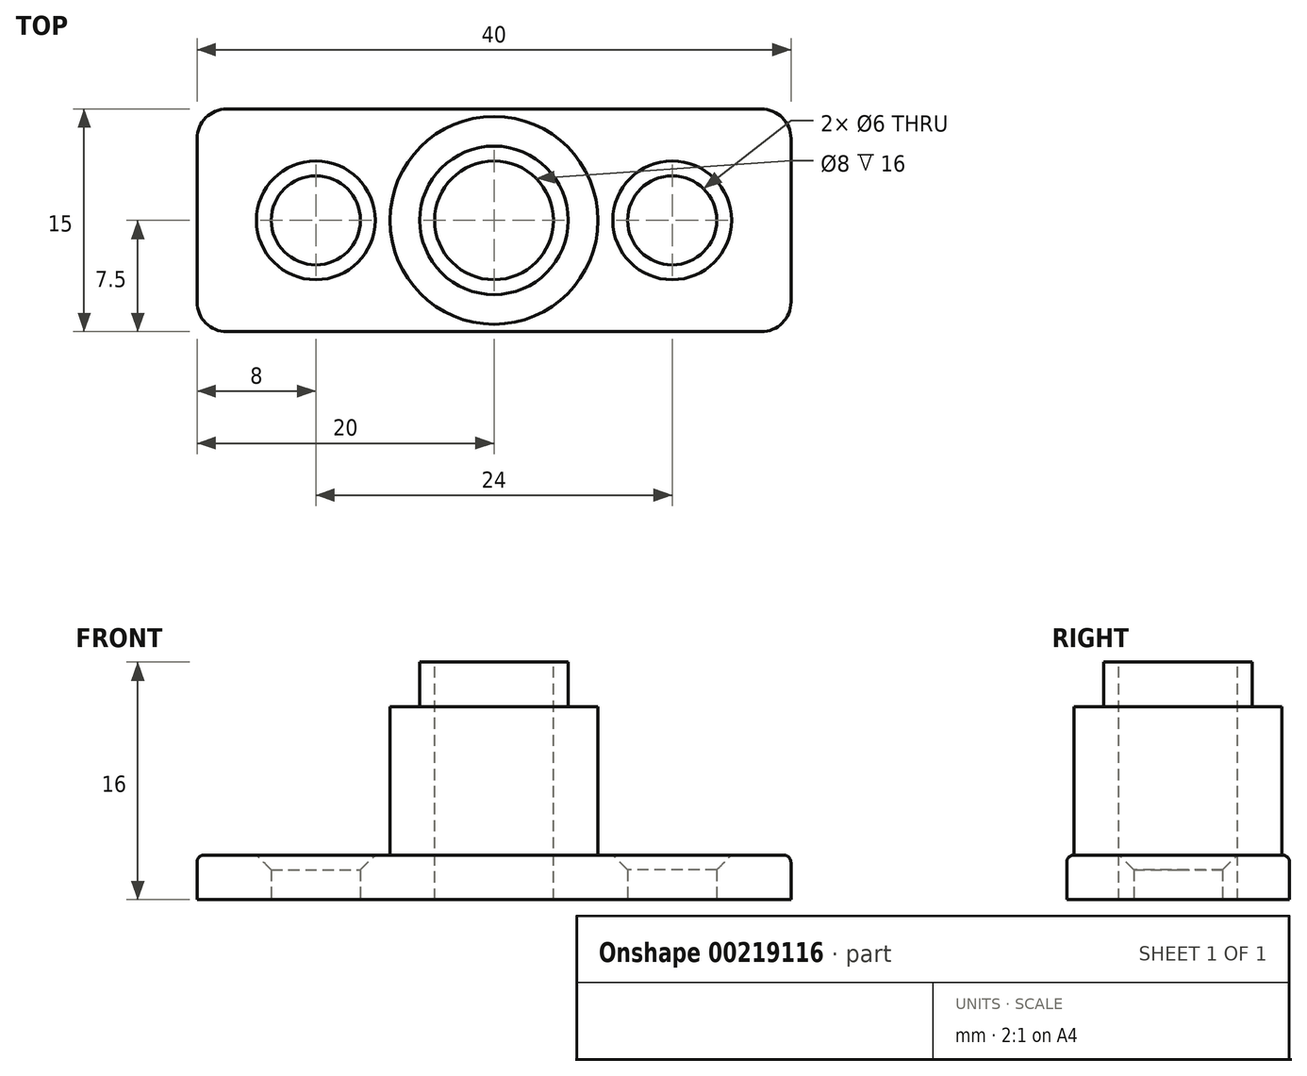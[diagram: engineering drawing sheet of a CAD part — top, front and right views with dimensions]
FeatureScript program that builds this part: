
annotation { "Feature Type Name" : "Feature", "Feature Type Description" : "" }
export const myFeature = defineFeature(function(context is Context, id is Id, definition is map)
    precondition{}
    {
        {
            var Q0;
            Q0=qCreatedBy(makeId("Top.planeOp"),FACE);
            var sketch = newSketch(context, id + "F0", { "sketchPlane" : qUnion([Q0])});
            skLineSegment(sketch, "E0.bottom", {"start": v(-20, 15) * mm, "end": v(0, 15) * mm});
            skLineSegment(sketch, "E0.top", {"start": v(-20, 0) * mm, "end": v(0, 0) * mm});
            skLineSegment(sketch, "E0.left", {"start": v(-20, 15) * mm, "end": v(-20, 0) * mm});
            skLineSegment(sketch, "E0.right", {"start": v(0, 15) * mm, "end": v(0, 0) * mm});
            skLineSegment(sketch, "E1", {"start": v(-20, 7.5) * mm, "end": v(0, 7.5) * mm, "construction": true});
            skSolve(sketch);
        }
        {
            var Q0;
            Q0=makeQuery(id+"F0.imprint","IMPRINT",FACE,{"disambiguationData":[TD([[makeQuery(id+"F0.imprint","IMPRINT",EDGE,{"derivedFrom":sQuery(id+"F0.wireOp",EDGE,"E0.bottom")}),-1.0]])]});
            extrude(context, id + "F1", {"entities" : qUnion([Q0]), "depth" : 3 * mm, "offsetDistance" : 25 * mm});
        }
        {
            var Q0;
            Q0=makeQuery(id+"F1.opExtrude","CAP_FACE",FACE,{"disambiguationData":[OSD([sQuery(id+"F0.wireOp",EDGE,"E0.bottom"),sQuery(id+"F0.wireOp",EDGE,"E0.top"),sQuery(id+"F0.wireOp",EDGE,"E0.left"),sQuery(id+"F0.wireOp",EDGE,"E0.right")])],"isStart":false});
            var sketch = newSketch(context, id + "F2", { "sketchPlane" : qUnion([Q0])});
            skArc(sketch, "E2", {"start": v(0, 14.5) * mm, "mid": v(-7, 7.5) * mm, "end": v(0, 0.5) * mm});
            skLineSegment(sketch, "E3", {"start": v(0, 0.5) * mm, "end": v(0, 14.5) * mm});
            skSolve(sketch);
        }
        {
            var Q0;
            Q0=makeQuery(id+"F2.imprint","IMPRINT",FACE,{"disambiguationData":[TD([[makeQuery(id+"F2.imprint","IMPRINT",EDGE,{"derivedFrom":sQuery(id+"F2.wireOp",EDGE,"E2")}),1.0]])]});
            extrude(context, id + "F3", {"entities" : qUnion([Q0]), "operationType" : NewBodyOperationType.ADD, "depth" : 10 * mm, "offsetDistance" : 25 * mm});
        }
        {
            var Q0;
            Q0=makeQuery(id+"F3.opExtrude","CAP_FACE",FACE,{"disambiguationData":[OSD([sQuery(id+"F2.wireOp",EDGE,"E2"),sQuery(id+"F2.wireOp",EDGE,"E3")])],"isStart":false});
            var sketch = newSketch(context, id + "F4", { "sketchPlane" : qUnion([Q0])});
            skArc(sketch, "E4", {"start": v(0, 12.5) * mm, "mid": v(-5, 7.5) * mm, "end": v(0, 2.5) * mm});
            skLineSegment(sketch, "E5", {"start": v(0, 12.5) * mm, "end": v(0, 2.5) * mm});
            skSolve(sketch);
        }
        {
            var Q0;
            Q0=makeQuery(id+"F4.imprint","IMPRINT",FACE,{"disambiguationData":[TD([[makeQuery(id+"F4.imprint","IMPRINT",EDGE,{"derivedFrom":sQuery(id+"F4.wireOp",EDGE,"E4")}),1.0]])]});
            extrude(context, id + "F5", {"entities" : qUnion([Q0]), "operationType" : NewBodyOperationType.ADD, "depth" : 3 * mm, "offsetDistance" : 25 * mm});
        }
        {
            var Q0;
            Q0=makeQuery(id+"F5.opExtrude","CAP_FACE",FACE,{"disambiguationData":[OSD([sQuery(id+"F4.wireOp",EDGE,"E4"),sQuery(id+"F4.wireOp",EDGE,"E5")])],"isStart":false});
            var sketch = newSketch(context, id + "F6", { "sketchPlane" : qUnion([Q0])});
            skArc(sketch, "E6", {"start": v(0, 11.5) * mm, "mid": v(-4, 7.5) * mm, "end": v(0, 3.5) * mm});
            skLineSegment(sketch, "E7", {"start": v(0, 3.5) * mm, "end": v(0, 11.5) * mm});
            skSolve(sketch);
        }
        {
            var Q0;
            Q0=makeQuery(id+"F6.imprint","IMPRINT",FACE,{"disambiguationData":[TD([[makeQuery(id+"F6.imprint","IMPRINT",EDGE,{"derivedFrom":sQuery(id+"F6.wireOp",EDGE,"E6")}),1.0]])]});
            extrude(context, id + "F7", {"entities" : qUnion([Q0]), "operationType" : NewBodyOperationType.REMOVE, "oppositeDirection" : true, "depth" : 25 * mm, "offsetDistance" : 25 * mm});
        }
        {
            var Q0;
            Q0=makeQuery(id+"F1.opExtrude","CAP_FACE",FACE,{"disambiguationData":[OSD([sQuery(id+"F0.wireOp",EDGE,"E0.bottom"),sQuery(id+"F0.wireOp",EDGE,"E0.top"),sQuery(id+"F0.wireOp",EDGE,"E0.left"),sQuery(id+"F0.wireOp",EDGE,"E0.right")])],"isStart":false});
            var sketch = newSketch(context, id + "F8", { "sketchPlane" : qUnion([Q0])});
            skCircle(sketch, "E8", {"center": v(-12, 7.5) * mm, "radius": 3 * mm});
            skSolve(sketch);
        }
        {
            var Q0;
            Q0=sQuery(id+"F8.wireOp",VERTEX,"E8.center");
            var Q1;
            Q1=makeQuery(id+"F1.opExtrude","SWEPT_BODY",BODY,{"disambiguationData":[OSD([sQuery(id+"F0.wireOp",EDGE,"E0.bottom"),sQuery(id+"F0.wireOp",EDGE,"E0.top"),sQuery(id+"F0.wireOp",EDGE,"E0.left"),sQuery(id+"F0.wireOp",EDGE,"E0.right")])]});
            hole(context, id + "F9", {"style" : HoleStyle.C_SINK, "endStyle" : HoleEndStyle.THROUGH, "holeDiameter" : 6 * mm, "cSinkDiameter" : 8 * mm, "cSinkAngle" : 90 * degree, "majorDiameter" : 5 * mm, "isTappedThrough" : true, "tappedDepth" : 12 * mm, "tapClearance" : 3, "locations" : qUnion([Q0]), "scope" : qUnion([Q1]), "startStyle" : HoleStartStyle.PART});
        }
        {
            var Q0;
            Q0=makeQuery(id+"F1.opExtrude","SWEPT_EDGE",EDGE,{"disambiguationData":[OSD([sQuery(id+"F0.wireOp",EDGE,"E0.top"),sQuery(id+"F0.wireOp",EDGE,"E0.left")])]});
            var Q1;
            Q1=makeQuery(id+"F1.opExtrude","SWEPT_EDGE",EDGE,{"disambiguationData":[OSD([sQuery(id+"F0.wireOp",EDGE,"E0.bottom"),sQuery(id+"F0.wireOp",EDGE,"E0.left")])]});
            fillet(context, id + "F10", {"entities" : qUnion([Q0, Q1]), "tangentPropagation" : true, "radius" : 2 * mm, "defaultsChanged" : true, "vertexSettings" : [], "allowEdgeOverflow" : false});
        }
        {
            var Q0;
            Q0=makeQuery(id+"F1.opExtrude","SWEPT_BODY",BODY,{"disambiguationData":[OSD([sQuery(id+"F0.wireOp",EDGE,"E0.bottom"),sQuery(id+"F0.wireOp",EDGE,"E0.top"),sQuery(id+"F0.wireOp",EDGE,"E0.left"),sQuery(id+"F0.wireOp",EDGE,"E0.right")])]});
            var Q1;
            Q1=qCreatedBy(makeId("Right.planeOp"),FACE);
            mirror(context, id + "F11", {"operationType" : NewBodyOperationType.ADD, "entities" : qUnion([Q0]), "mirrorPlane" : qUnion([Q1])});
        }
        {
            var Q0;
            {var subQ0=makeQuery(id+"F1.opExtrude","CAP_EDGE",EDGE,{"disambiguationData":[OSD([sQuery(id+"F0.wireOp",EDGE,"E0.top")])],"isStart":false});Q0=makeQuery(id+"F11.boolean.opBoolean","MERGE",EDGE,{"derivedFrom":[subQ0,makeQuery(id+"F11.opPattern","COPY",EDGE,{"derivedFrom":subQ0,"instanceName":"1"})]});}
            fillet(context, id + "F12", {"entities" : qUnion([Q0]), "tangentPropagation" : true, "radius" : 0.5 * mm, "defaultsChanged" : true, "vertexSettings" : [], "allowEdgeOverflow" : false});
        }
    });
